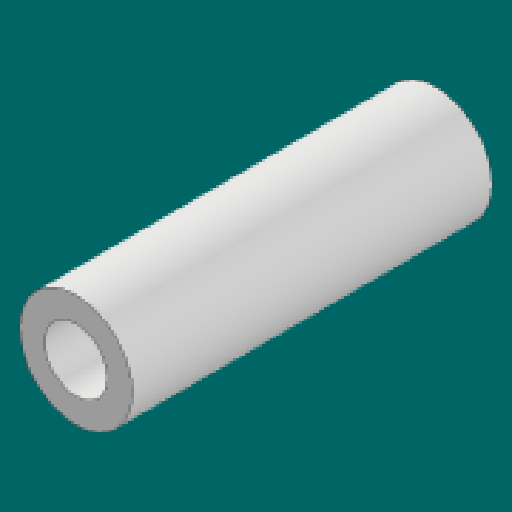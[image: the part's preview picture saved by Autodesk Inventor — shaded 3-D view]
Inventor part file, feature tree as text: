
AUTODESK INVENTOR PART (.ipt)
format: ipt  version: 2023.1 (Build 271208000, 208)  size: 99,328 bytes
history: native  units: in
note: dims shown in document units (in); Inventor stores cm internally (conversion verified against a paired STEP export)
features: extrude x1, sketch x1
ambient origin geometry x8: Origin, YZ Plane, XZ Plane, XY Plane, X Axis, Y Axis, Z Axis, Center Point
bodies: Solid1 (feature_tree)
feature tree (2):
  extrude  "Extrusion1"  Depth=1.2in
  sketch  "Sketch1"  dims[d0=0.21in d1=0.375in d2=1.2in d3=0.0in]
